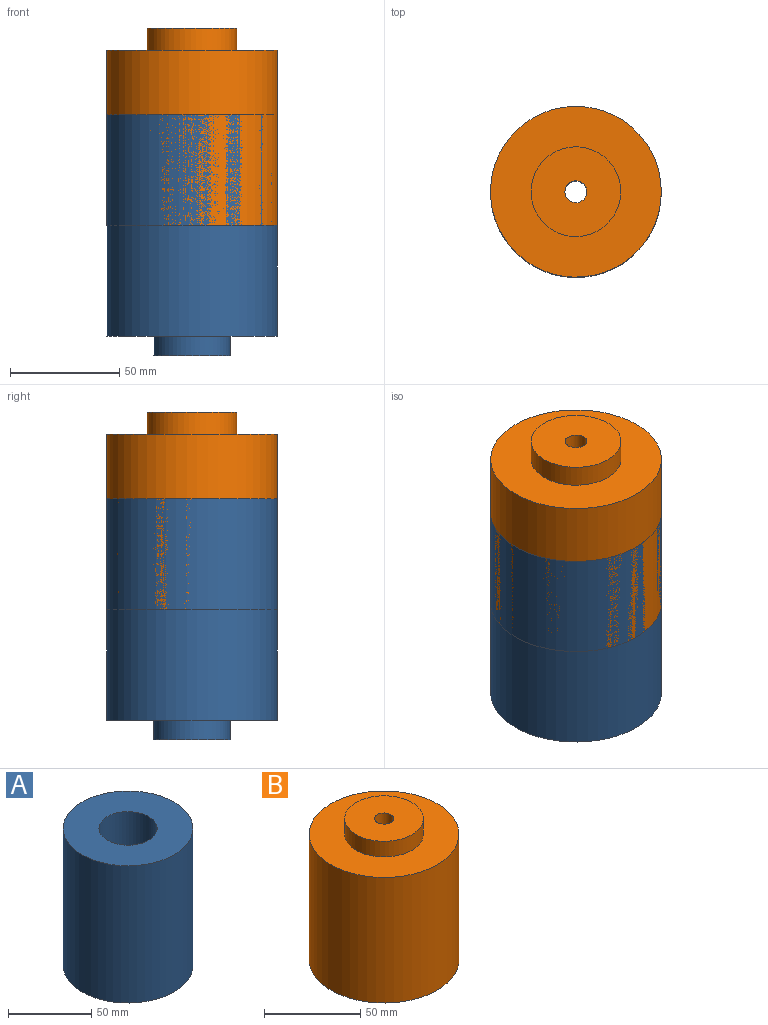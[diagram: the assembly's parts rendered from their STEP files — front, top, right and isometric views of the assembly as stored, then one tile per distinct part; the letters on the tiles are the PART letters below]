
ASSEMBLY  parts=2 mates=1
PART A: 8 faces, bbox 78x78x110 mm
  f0: cylinder r=17.5mm len=35mm, axis (0,0,-1), area 989.6mm2, adj f3,f7
  f1: cylinder r=5mm len=10mm, axis (0,0,-1), area 314.2mm2, adj f2,f3
  f2: plane 35x35mm, normal (0,0,1), area 883.6mm2, adj f1,f4
  f3: plane 35x35mm, normal (0,0,-1), area 883.6mm2, adj f0,f1
  f4: cylinder r=17.5mm len=100mm, axis (0,0,-1), area 10995.6mm2, adj f2,f6
  f5: cylinder r=39mm len=101mm, axis (0,0,-1), area 24749.5mm2, adj f6,f7
  f6: plane 78x78mm, normal (0,0,1), area 3816.2mm2, adj f4,f5
  f7: plane 78x78mm, normal (0,0,-1), area 3816.2mm2, adj f0,f5
PART B: 6 faces, bbox 78x78x90 mm
  f0: cylinder r=39mm len=80mm, axis (0,0,-1), area 19603.5mm2, adj f1,f2
  f1: plane 78x78mm, normal (0,0,1), area 3458.1mm2, adj f0,f3
  f2: plane 78x78mm, normal (0,0,-1), area 4699.8mm2, adj f0,f4
  f3: cylinder r=20.5mm len=41mm, axis (0,0,-1), area 1288.1mm2, adj f1,f5
  f4: cylinder r=5mm len=90mm, axis (0,0,-1), area 2827.4mm2, adj f2,f5
  f5: plane 41x41mm, normal (0,0,1), area 1241.7mm2, adj f3,f4
PLACE A t=(-85.85,-55.59,26.73)mm
PLACE B t=(-85.85,-55.59,-23.7)mm
MATE cylindrical A.f0 <-> B.f0  axis (0,0,1) through (-85.85,-55.59,136.73)mm
